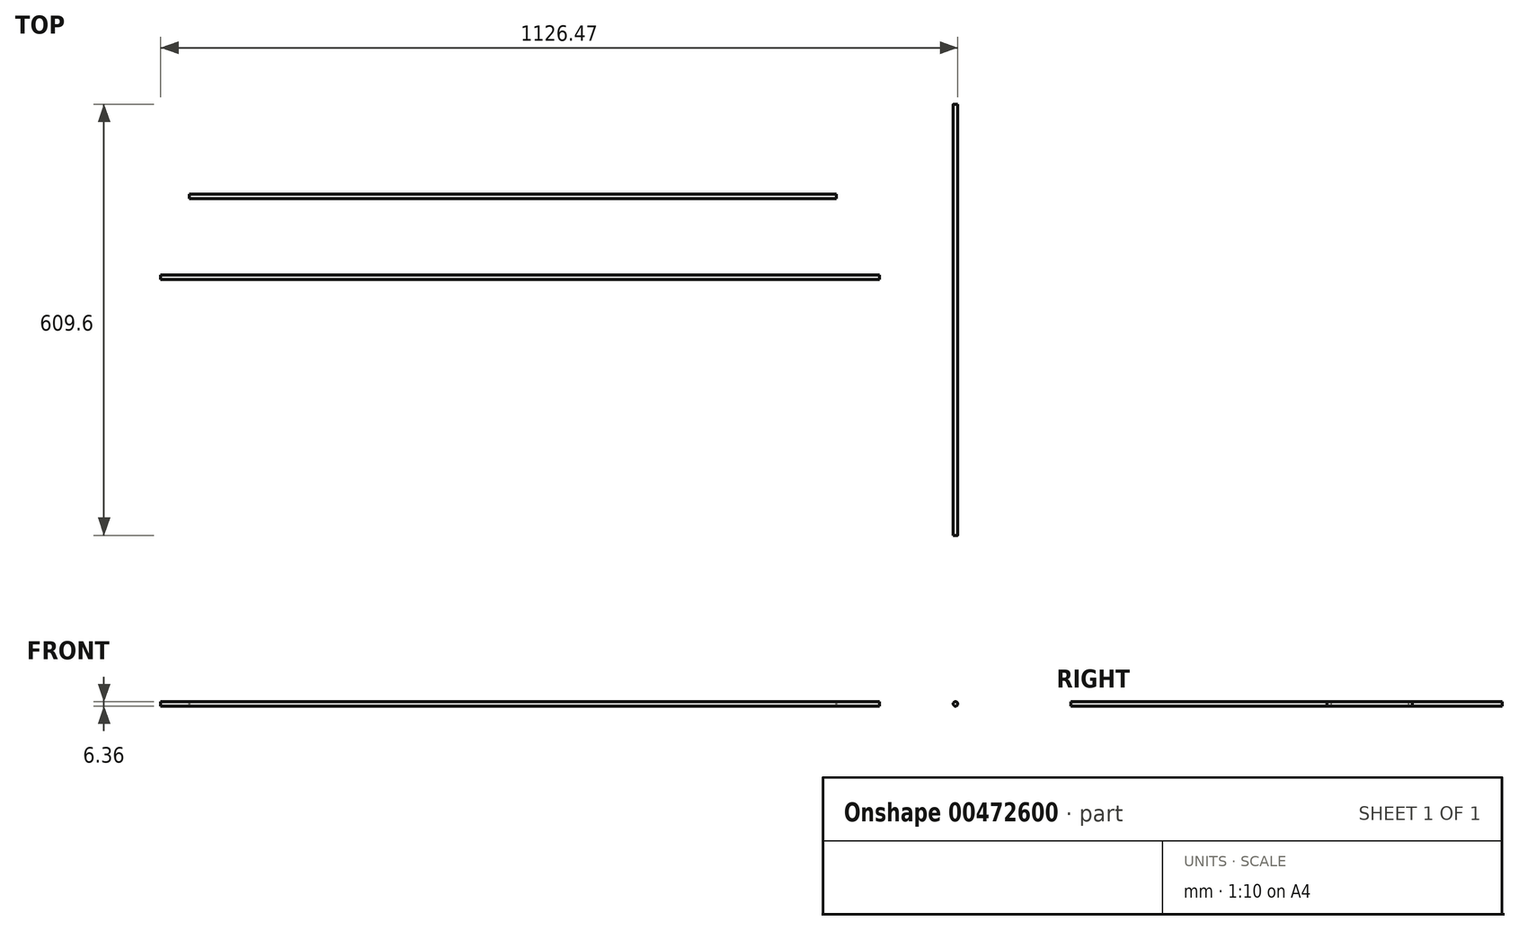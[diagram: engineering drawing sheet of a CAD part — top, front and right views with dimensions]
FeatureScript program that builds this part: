
annotation { "Feature Type Name" : "Feature", "Feature Type Description" : "" }
export const myFeature = defineFeature(function(context is Context, id is Id, definition is map)
    precondition{}
    {
        {
            var Q0;
            Q0=qCreatedBy(makeId("Top.planeOp"),FACE);
            var sketch = newSketch(context, id + "F0", { "sketchPlane" : qUnion([Q0])});
            skLineSegment(sketch, "E0.bottom", {"start": v(-491.41, -36.26) * mm, "end": v(524.59, -36.26) * mm});
            skLineSegment(sketch, "E0.top", {"start": v(-491.41, -33.08) * mm, "end": v(524.59, -33.08) * mm});
            skLineSegment(sketch, "E0.left", {"start": v(-491.41, -36.26) * mm, "end": v(-491.41, -33.08) * mm});
            skLineSegment(sketch, "E0.right", {"start": v(524.59, -36.26) * mm, "end": v(524.59, -33.08) * mm});
            skSolve(sketch);
        }
        {
            var Q0;
            Q0=makeQuery(id+"F0.imprint","IMPRINT",FACE,{"disambiguationData":[TD([[makeQuery(id+"F0.imprint","IMPRINT",EDGE,{"derivedFrom":sQuery(id+"F0.wireOp",EDGE,"E0.bottom")}),1.0]])]});
            var Q1;
            Q1=sQuery(id+"F0.wireOp",EDGE,"E0.bottom");
            revolve(context, id + "F1", {"entities" : qUnion([Q0]), "axis" : qUnion([Q1]), "revolveType" : RevolveType.FULL});
        }
        {
            var Q0;
            Q0=qCreatedBy(makeId("Top.planeOp"),FACE);
            var sketch = newSketch(context, id + "F2", { "sketchPlane" : qUnion([Q0])});
            skLineSegment(sketch, "E1.bottom", {"start": v(-450.94, 75.15) * mm, "end": v(463.46, 75.15) * mm});
            skLineSegment(sketch, "E1.top", {"start": v(-450.94, 78.32) * mm, "end": v(463.46, 78.32) * mm});
            skLineSegment(sketch, "E1.left", {"start": v(-450.94, 75.15) * mm, "end": v(-450.94, 78.32) * mm});
            skLineSegment(sketch, "E1.right", {"start": v(463.46, 75.15) * mm, "end": v(463.46, 78.32) * mm});
            skSolve(sketch);
        }
        {
            var Q0;
            Q0=qCreatedBy(makeId("Top.planeOp"),FACE);
            var sketch = newSketch(context, id + "F3", { "sketchPlane" : qUnion([Q0])});
            skLineSegment(sketch, "E2.bottom", {"start": v(-306.45, 134.2) * mm, "end": v(506.35, 134.2) * mm});
            skLineSegment(sketch, "E2.top", {"start": v(-306.45, 137.38) * mm, "end": v(506.35, 137.38) * mm});
            skLineSegment(sketch, "E2.left", {"start": v(-306.45, 134.2) * mm, "end": v(-306.45, 137.38) * mm});
            skLineSegment(sketch, "E2.right", {"start": v(506.35, 134.2) * mm, "end": v(506.35, 137.38) * mm});
            skSolve(sketch);
        }
        {
            var Q0;
            Q0=qCreatedBy(makeId("Top.planeOp"),FACE);
            var sketch = newSketch(context, id + "F4", { "sketchPlane" : qUnion([Q0])});
            skLineSegment(sketch, "E3.bottom", {"start": v(-256.94, 175.31) * mm, "end": v(505.06, 175.31) * mm});
            skLineSegment(sketch, "E3.top", {"start": v(-256.94, 178.49) * mm, "end": v(505.06, 178.49) * mm});
            skLineSegment(sketch, "E3.left", {"start": v(-256.94, 175.31) * mm, "end": v(-256.94, 178.49) * mm});
            skLineSegment(sketch, "E3.right", {"start": v(505.06, 175.31) * mm, "end": v(505.06, 178.49) * mm});
            skSolve(sketch);
        }
        {
            var Q0;
            Q0=makeQuery(id+"F2.imprint","IMPRINT",FACE,{"disambiguationData":[TD([[makeQuery(id+"F2.imprint","IMPRINT",EDGE,{"derivedFrom":sQuery(id+"F2.wireOp",EDGE,"E1.bottom")}),1.0]])]});
            var Q1;
            Q1=sQuery(id+"F2.wireOp",EDGE,"E1.top");
            revolve(context, id + "F5", {"entities" : qUnion([Q0]), "axis" : qUnion([Q1]), "revolveType" : RevolveType.FULL});
        }
        {
            var Q0;
            Q0=makeQuery(id+"F3.imprint","IMPRINT",FACE,{"disambiguationData":[TD([[makeQuery(id+"F3.imprint","IMPRINT",EDGE,{"derivedFrom":sQuery(id+"F3.wireOp",EDGE,"E2.bottom")}),1.0]])]});
            var Q1;
            Q1=sQuery(id+"F3.wireOp",EDGE,"E2.top");
            revolve(context, id + "F6", {"entities" : qUnion([Q0]), "axis" : qUnion([Q1]), "revolveType" : RevolveType.FULL});
        }
        {
            var Q0;
            Q0=makeQuery(id+"F4.imprint","IMPRINT",FACE,{"disambiguationData":[TD([[makeQuery(id+"F4.imprint","IMPRINT",EDGE,{"derivedFrom":sQuery(id+"F4.wireOp",EDGE,"E3.bottom")}),1.0]])]});
            var Q1;
            Q1=sQuery(id+"F4.wireOp",EDGE,"E3.top");
            revolve(context, id + "F7", {"entities" : qUnion([Q0]), "axis" : qUnion([Q1]), "revolveType" : RevolveType.FULL});
        }
        {
            var Q0;
            Q0=qCreatedBy(makeId("Top.planeOp"),FACE);
            var sketch = newSketch(context, id + "F8", { "sketchPlane" : qUnion([Q0])});
            skLineSegment(sketch, "E4.bottom", {"start": v(628.7, 208.3) * mm, "end": v(631.88, 208.3) * mm});
            skLineSegment(sketch, "E4.top", {"start": v(628.7, -401.3) * mm, "end": v(631.88, -401.3) * mm});
            skLineSegment(sketch, "E4.left", {"start": v(628.7, 208.3) * mm, "end": v(628.7, -401.3) * mm});
            skLineSegment(sketch, "E4.right", {"start": v(631.88, 208.3) * mm, "end": v(631.88, -401.3) * mm});
            skSolve(sketch);
        }
        {
            var Q0;
            Q0=qCreatedBy(makeId("Top.planeOp"),FACE);
            var sketch = newSketch(context, id + "F9", { "sketchPlane" : qUnion([Q0])});
            skLineSegment(sketch, "E5.bottom", {"start": v(710.22, 388.58) * mm, "end": v(713.4, 388.58) * mm});
            skLineSegment(sketch, "E5.top", {"start": v(710.22, -525.82) * mm, "end": v(713.4, -525.82) * mm});
            skLineSegment(sketch, "E5.left", {"start": v(710.22, 388.58) * mm, "end": v(710.22, -525.82) * mm});
            skLineSegment(sketch, "E5.right", {"start": v(713.4, 388.58) * mm, "end": v(713.4, -525.82) * mm});
            skSolve(sketch);
        }
        {
            var Q0;
            Q0=makeQuery(id+"F8.imprint","IMPRINT",FACE,{"disambiguationData":[TD([[makeQuery(id+"F8.imprint","IMPRINT",EDGE,{"derivedFrom":sQuery(id+"F8.wireOp",EDGE,"E4.bottom")}),-1.0]])]});
            var Q1;
            Q1=sQuery(id+"F8.wireOp",EDGE,"E4.right");
            revolve(context, id + "F10", {"entities" : qUnion([Q0]), "axis" : qUnion([Q1]), "revolveType" : RevolveType.FULL});
        }
        {
            var Q0;
            Q0=makeQuery(id+"F9.imprint","IMPRINT",FACE,{"disambiguationData":[TD([[makeQuery(id+"F9.imprint","IMPRINT",EDGE,{"derivedFrom":sQuery(id+"F9.wireOp",EDGE,"E5.bottom")}),-1.0]])]});
            var Q1;
            Q1=sQuery(id+"F9.wireOp",EDGE,"E5.right");
            revolve(context, id + "F11", {"entities" : qUnion([Q0]), "axis" : qUnion([Q1]), "revolveType" : RevolveType.FULL});
        }
        {
            var Q0;
            Q0=makeQuery(id+"F11.opRevolve","SWEPT_BODY",BODY,{"disambiguationData":[OSD([sQuery(id+"F9.wireOp",EDGE,"E5.bottom"),sQuery(id+"F9.wireOp",EDGE,"E5.top"),sQuery(id+"F9.wireOp",EDGE,"E5.left"),sQuery(id+"F9.wireOp",EDGE,"E5.right")])]});
            deleteBodies(context, id + "F12", {"entities" : qUnion([Q0])});
        }
        {
            var Q0;
            Q0=makeQuery(id+"F6.opRevolve","SWEPT_BODY",BODY,{"disambiguationData":[OSD([sQuery(id+"F3.wireOp",EDGE,"E2.bottom"),sQuery(id+"F3.wireOp",EDGE,"E2.top"),sQuery(id+"F3.wireOp",EDGE,"E2.left"),sQuery(id+"F3.wireOp",EDGE,"E2.right")])]});
            deleteBodies(context, id + "F13", {"entities" : qUnion([Q0])});
        }
        {
            var Q0;
            Q0=makeQuery(id+"F7.opRevolve","SWEPT_BODY",BODY,{"disambiguationData":[OSD([sQuery(id+"F4.wireOp",EDGE,"E3.bottom"),sQuery(id+"F4.wireOp",EDGE,"E3.top"),sQuery(id+"F4.wireOp",EDGE,"E3.left"),sQuery(id+"F4.wireOp",EDGE,"E3.right")])]});
            deleteBodies(context, id + "F14", {"entities" : qUnion([Q0])});
        }
    });
